# Revit family: 202_VIP-_S
name_source: partatom
category: Air Terminals
units: mm (PartAtom-declared; Revit-internal decimal feet)

## family parameters
Always vertical = Yes
Cut with Voids When Loaded = No
Part Type = Normal
Room Calculation Point = Yes
Round Connector Dimension = Use Diameter
Shared = No
Work Plane-Based = No

## types (2) — shared parameters
C = 12 mm  [stored 0.0393701 ft]
CAT0 = Yes
CL_Location_5000 = 5000 mm  [stored 16.4042 ft]
C__ve = -12 mm  [stored -0.0393701 ft]
D1 = 8 mm  [stored 0.0262467 ft]
Description = Extract valve
E = 38 mm  [stored 0.124672 ft]
E1 = 35 mm  [stored 0.114829 ft]
H1 = 18 mm  [stored 0.0590551 ft]
H1__ve = -18 mm  [stored -0.0590551 ft]
L_ARR = 400 mm  [stored 1.31234 ft]
Manufacturer = Climecon
QmdConnectorList = 201;D
R2 = 3 mm  [stored 0.00984252 ft]
T1 = Yes
URL = www.climecon.fi
W_ARR = 400 mm  [stored 1.31234 ft]
X1 = 10 mm  [stored 0.0328084 ft]
XRefLineVPlnId = 7453
YRefLineVPlnId = 7456
magiPartTypeId = 202
magiProductFamilyId = VIP-*S
zero-valued in all types: CLBTZ, H_ARR, MC_Default_elevation

## per-type parameters (varying)
| type | A1 | AA | D | R |
| VIP-100S | 46 mm | 70 mm  [stored 0.229659 ft] | 100 mm | 50 mm  [stored 0.164042 ft] |
| VIP-125S | 54 mm | 83 mm | 125 mm | 63 mm |

note: column(s) folded — value = type name in every type: magiProductCode, magiProductId

note: [stored X ft] marks values corroborated as IEEE doubles in the binary element streams (Revit-internal decimal feet)

## geometry (parser evidence)
native form markers: Sweep x2
no freeform markers — native parametric forms only
